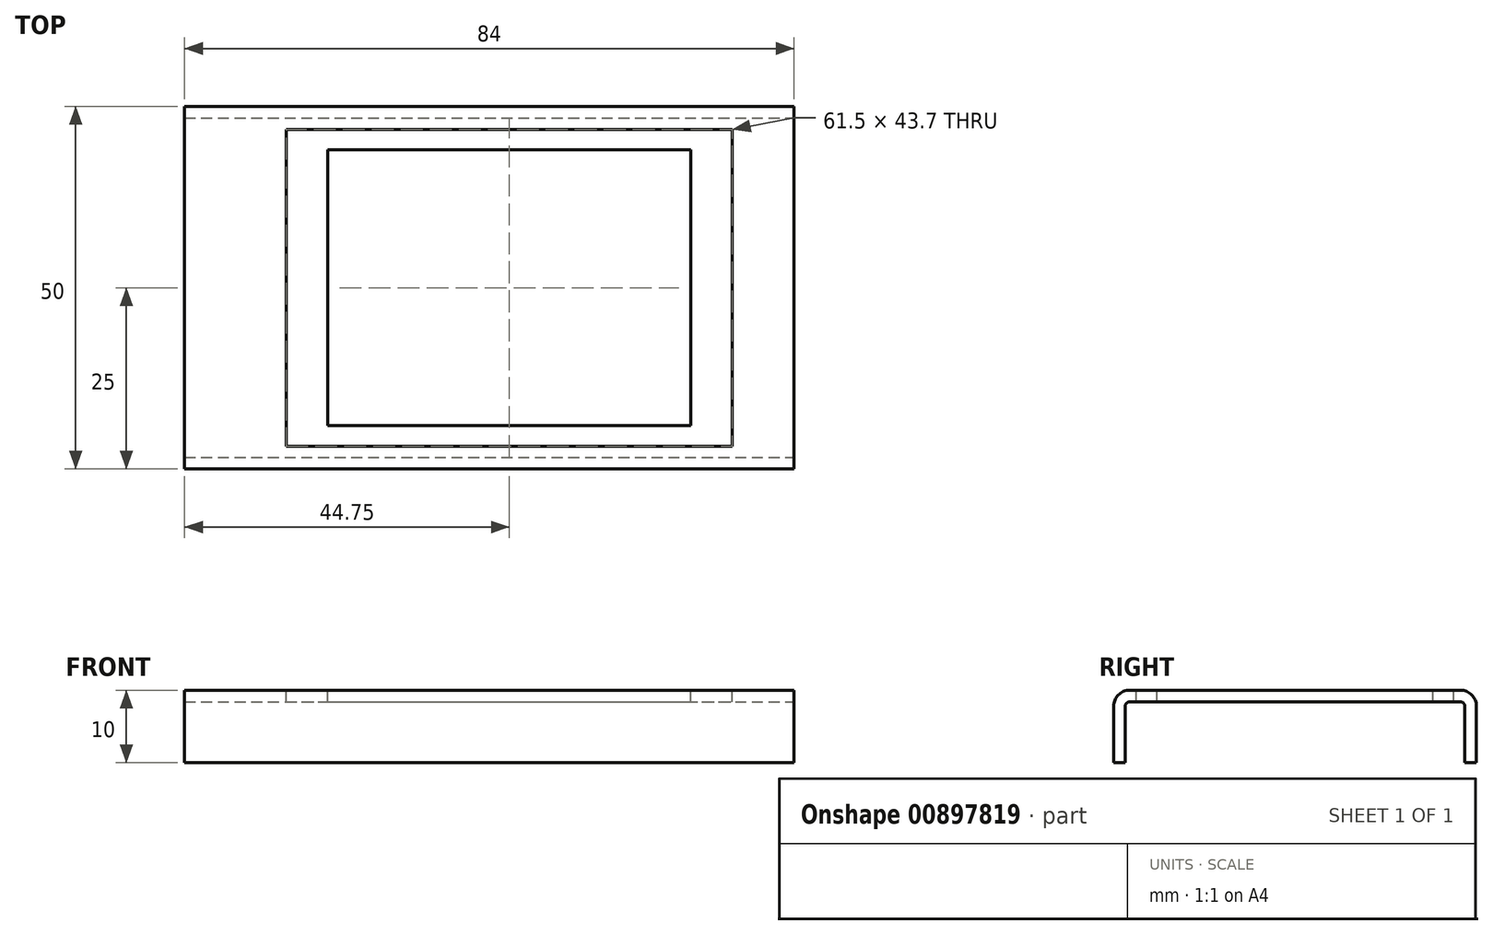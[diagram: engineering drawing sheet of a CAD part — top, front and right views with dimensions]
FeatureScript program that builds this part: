
annotation { "Feature Type Name" : "Feature", "Feature Type Description" : "" }
export const myFeature = defineFeature(function(context is Context, id is Id, definition is map)
    precondition{}
    {
        {
            var Q0;
            Q0=qCreatedBy(makeId("Right.planeOp"),FACE);
            var sketch = newSketch(context, id + "F0", { "sketchPlane" : qUnion([Q0])});
            skLineSegment(sketch, "E0.bottom", {"start": v(2.2, 20) * mm, "end": v(47.8, 20) * mm});
            skLineSegment(sketch, "E0.left", {"start": v(0, 17.8) * mm, "end": v(0, 10) * mm});
            skLineSegment(sketch, "E0.right", {"start": v(50, 17.8) * mm, "end": v(50, 10) * mm});
            skPoint(sketch, "E1.visualSharp", {"position": v(0, 20) * mm});
            skArc(sketch, "E1.filletArc", {"start": v(2.2, 20) * mm, "mid": v(0.64, 19.36) * mm, "end": v(0, 17.8) * mm});
            skPoint(sketch, "E2.visualSharp", {"position": v(50, 20) * mm});
            skArc(sketch, "E2.filletArc", {"start": v(50, 17.8) * mm, "mid": v(49.36, 19.36) * mm, "end": v(47.8, 20) * mm});
            skPoint(sketch, "E3.visualSharp", {"position": v(50, 0) * mm});
            skPoint(sketch, "E4.visualSharp", {"position": v(0, 0) * mm});
            skArc(sketch, "E5.0", {"start": v(48.4, 17.8) * mm, "mid": v(48.22, 18.22) * mm, "end": v(47.8, 18.4) * mm});
            skLineSegment(sketch, "E5.1", {"start": v(2.2, 18.4) * mm, "end": v(47.8, 18.4) * mm});
            skLineSegment(sketch, "E5.2", {"start": v(48.4, 17.8) * mm, "end": v(48.4, 10) * mm});
            skArc(sketch, "E5.3", {"start": v(2.2, 18.4) * mm, "mid": v(1.78, 18.22) * mm, "end": v(1.6, 17.8) * mm});
            skLineSegment(sketch, "E5.7", {"start": v(1.6, 17.8) * mm, "end": v(1.6, 10) * mm});
            skLineSegment(sketch, "E6", {"start": v(48.4, 10) * mm, "end": v(50, 10) * mm});
            skLineSegment(sketch, "E7", {"start": v(0, 10) * mm, "end": v(1.6, 10) * mm});
            skSolve(sketch);
        }
        {
            var Q0;
            Q0=makeQuery(id+"F0.imprint","IMPRINT",FACE,{"disambiguationData":[TD([[makeQuery(id+"F0.imprint","IMPRINT",EDGE,{"derivedFrom":sQuery(id+"F0.wireOp",EDGE,"E0.bottom")}),-1.0]])]});
            extrude(context, id + "F1", {"entities" : qUnion([Q0]), "oppositeDirection" : true, "depth" : 84 * mm, "offsetDistance" : 25 * mm});
        }
        {
            var Q0;
            Q0=makeQuery(id+"F1.opExtrude","SWEPT_FACE",FACE,{"disambiguationData":[OSD([sQuery(id+"F0.wireOp",EDGE,"E0.bottom")])]});
            var sketch = newSketch(context, id + "F2", { "sketchPlane" : qUnion([Q0])});
            skLineSegment(sketch, "E8.bottom", {"start": v(-70, 46.85) * mm, "end": v(-8.5, 46.85) * mm});
            skLineSegment(sketch, "E8.top", {"start": v(-70, 3.15) * mm, "end": v(-8.5, 3.15) * mm});
            skLineSegment(sketch, "E8.left", {"start": v(-70, 46.85) * mm, "end": v(-70, 3.15) * mm});
            skLineSegment(sketch, "E8.right", {"start": v(-8.5, 46.85) * mm, "end": v(-8.5, 3.15) * mm});
            skLineSegment(sketch, "E9.bottom", {"start": v(-64.25, 44) * mm, "end": v(-14.25, 44) * mm});
            skLineSegment(sketch, "E9.top", {"start": v(-64.25, 6) * mm, "end": v(-14.25, 6) * mm});
            skLineSegment(sketch, "E9.left", {"start": v(-64.25, 44) * mm, "end": v(-64.25, 6) * mm});
            skLineSegment(sketch, "E9.right", {"start": v(-14.25, 44) * mm, "end": v(-14.25, 6) * mm});
            skLineSegment(sketch, "E10.bottom", {"start": v(-48.26, 44) * mm, "end": v(-24.2, 44) * mm});
            skLineSegment(sketch, "E10.top", {"start": v(-48.26, 44) * mm, "end": v(-24.2, 44) * mm});
            skLineSegment(sketch, "E10.left", {"start": v(-48.26, 44) * mm, "end": v(-48.26, 44) * mm});
            skLineSegment(sketch, "E10.right", {"start": v(-24.2, 44) * mm, "end": v(-24.2, 44) * mm});
            skSolve(sketch);
        }
        {
            var Q0;
            Q0=makeQuery(id+"F2.imprint","IMPRINT",FACE,{"disambiguationData":[TD([[makeQuery(id+"F2.imprint","IMPRINT",EDGE,{"derivedFrom":sQuery(id+"F2.wireOp",EDGE,"E8.bottom")}),-1.0]])]});
            extrude(context, id + "F3", {"entities" : qUnion([Q0]), "operationType" : NewBodyOperationType.REMOVE, "endBound" : BoundingType.UP_TO_NEXT, "oppositeDirection" : true, "depth" : 25 * mm, "offsetDistance" : 25 * mm});
        }
    });
